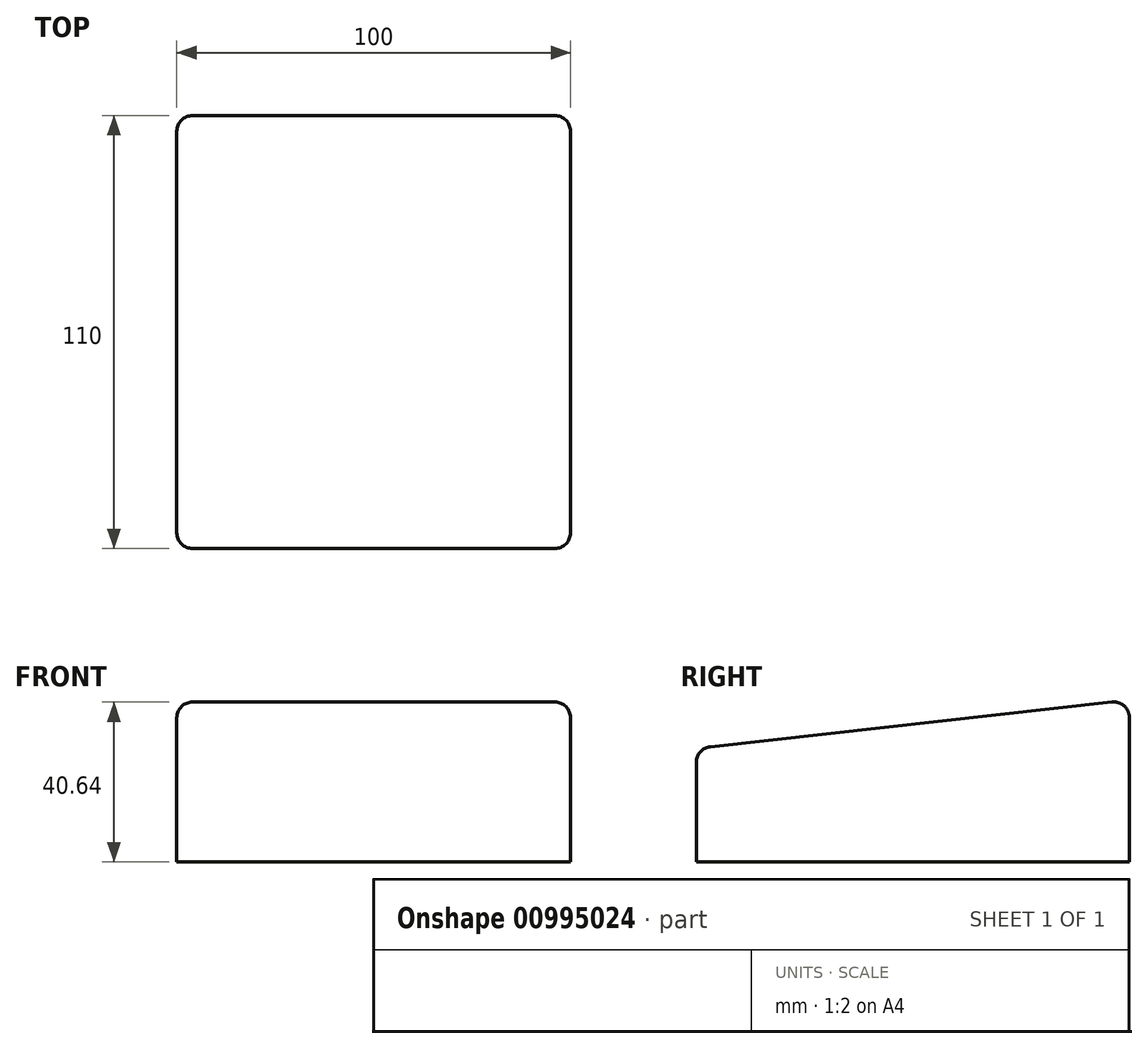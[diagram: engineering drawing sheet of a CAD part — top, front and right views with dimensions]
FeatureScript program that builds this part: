
annotation { "Feature Type Name" : "Feature", "Feature Type Description" : "" }
export const myFeature = defineFeature(function(context is Context, id is Id, definition is map)
    precondition{}
    {
        {
            var Q0;
            Q0=qCreatedBy(makeId("Right.planeOp"),FACE);
            var sketch = newSketch(context, id + "F0", { "sketchPlane" : qUnion([Q0])});
            skLineSegment(sketch, "E0", {"start": v(-55, 0) * mm, "end": v(55, 0) * mm});
            skLineSegment(sketch, "E1", {"start": v(55, 0) * mm, "end": v(55, 41.11) * mm});
            skLineSegment(sketch, "E2", {"start": v(55, 41.11) * mm, "end": v(-55, 28.89) * mm});
            skLineSegment(sketch, "E3", {"start": v(-55, 28.89) * mm, "end": v(-55, 0) * mm});
            skPoint(sketch, "E4", {"position": v(45, 40) * mm});
            skPoint(sketch, "E5", {"position": v(-45, 30) * mm});
            skPoint(sketch, "E6", {"position": v(0, 0) * mm});
            skLineSegment(sketch, "E7.0", {"start": v(55.22, 39.12) * mm, "end": v(-54.78, 26.9) * mm, "construction": true});
            skSolve(sketch);
        }
        {
            var Q0;
            Q0=qCreatedBy(makeId("Right.planeOp"),FACE);
            var sketch = newSketch(context, id + "F1", { "sketchPlane" : qUnion([Q0])});
            skCircle(sketch, "E8", {"center": v(7, 28.5) * mm, "radius": 27.5 * mm});
            skLineSegment(sketch, "E9", {"start": v(7, 28.5) * mm, "end": v(43.16, 27.87) * mm});
            skLineSegment(sketch, "E10", {"start": v(30.75, 37.09) * mm, "end": v(50.45, 36.74) * mm});
            skLineSegment(sketch, "E11", {"start": v(26.94, 18.15) * mm, "end": v(48.11, 17.78) * mm});
            skArc(sketch, "E12", {"start": v(32.12, 12.29) * mm, "mid": v(36.9, 29.25) * mm, "end": v(31.28, 45.94) * mm, "construction": true});
            skLineSegment(sketch, "E13", {"start": v(40.45, 36.92) * mm, "end": v(40.12, 17.92) * mm, "construction": true});
            skPoint(sketch, "E14", {"position": v(34.5, 28.02) * mm});
            skLineSegment(sketch, "E15", {"start": v(42.05, 36.89) * mm, "end": v(41.72, 17.9) * mm, "construction": true});
            skLineSegment(sketch, "E16", {"start": v(7, 28.5) * mm, "end": v(7, 15.35) * mm});
            skLineSegment(sketch, "E17", {"start": v(34.5, 28.02) * mm, "end": v(34.6, 33.85) * mm, "construction": true});
            skSolve(sketch);
        }
        {
            var Q0;
            Q0=sQuery(id+"F1.wireOp",VERTEX,"E9.start");
            var Q1;
            Q1=qCreatedBy(makeId("Top.planeOp"),FACE);
            cPlane(context, id + "F2", {"entities" : qUnion([Q0, Q1]), "cplaneType" : CPlaneType.PLANE_POINT, "offset" : 25 * mm, "width" : 150 * mm, "height" : 150 * mm});
        }
        {
            var Q0;
            Q0=sQuery(id+"F0.wireOp",EDGE,"E2");
            cPlane(context, id + "F3", {"entities" : qUnion([Q0]), "cplaneType" : CPlaneType.LINE_ANGLE, "offset" : 25 * mm, "angle" : 0 * degree, "width" : 150 * mm, "height" : 150 * mm});
        }
        {
            var Q0;
            Q0=qCreatedBy(id+"F3.planeOp",FACE);
            var sketch = newSketch(context, id + "F4", { "sketchPlane" : qUnion([Q0])});
            skLineSegment(sketch, "E18.bottom", {"start": v(-50, -59.2) * mm, "end": v(50, -59.2) * mm});
            skLineSegment(sketch, "E18.top", {"start": v(-50, 51.47) * mm, "end": v(50, 51.47) * mm});
            skLineSegment(sketch, "E18.left", {"start": v(-50, -59.2) * mm, "end": v(-50, 51.47) * mm});
            skLineSegment(sketch, "E18.right", {"start": v(50, -59.2) * mm, "end": v(50, 51.47) * mm});
            skPoint(sketch, "E19", {"position": v(0, 51.47) * mm});
            skSolve(sketch);
        }
        {
            var Q0;
            Q0=qCreatedBy(makeId("Front.planeOp"),FACE);
            var Q1;
            Q1=sQuery(id+"F1.wireOp",VERTEX,"E9.start");
            cPlane(context, id + "F5", {"entities" : qUnion([Q0, Q1]), "cplaneType" : CPlaneType.PLANE_POINT, "offset" : 25 * mm, "width" : 150 * mm, "height" : 150 * mm});
        }
        {
            var Q0;
            Q0=qCreatedBy(makeId("Top.planeOp"),FACE);
            var Q1;
            Q1=qCreatedBy(makeId("Origin.pointOp"),VERTEX);
            cPlane(context, id + "F6", {"entities" : qUnion([Q0, Q1]), "cplaneType" : CPlaneType.PLANE_POINT, "offset" : 25 * mm, "width" : 150 * mm, "height" : 150 * mm});
        }
        {
            var Q0;
            Q0=qCreatedBy(id+"F6.planeOp",FACE);
            var sketch = newSketch(context, id + "F7", { "sketchPlane" : qUnion([Q0])});
            skLineSegment(sketch, "E20.0.0", {"start": v(50, -55) * mm, "end": v(-50, -55) * mm});
            skLineSegment(sketch, "E20.0.1", {"start": v(-50, -55) * mm, "end": v(-50, 55) * mm});
            skLineSegment(sketch, "E20.0.2", {"start": v(-50, 55) * mm, "end": v(50, 55) * mm});
            skLineSegment(sketch, "E20.0.3", {"start": v(50, 55) * mm, "end": v(50, -55) * mm});
            skSolve(sketch);
        }
        {
            var Q0;
            Q0=qSketchRegion(id+"F0",true);
            var Q1;
            Q1=sQuery(id+"F7.wireOp",VERTEX,"E20.0.0.start");
            var Q2;
            Q2=sQuery(id+"F7.wireOp",VERTEX,"E20.0.0.end");
            extrude(context, id + "F8", {"entities" : qUnion([Q0]), "endBound" : BoundingType.UP_TO_VERTEX, "depth" : 25 * mm, "endBoundEntityVertex" : qUnion([Q1]), "offsetDistance" : 25 * mm, "hasSecondDirection" : true, "secondDirectionBound" : SecondDirectionBoundingType.UP_TO_VERTEX, "secondDirectionOppositeDirection" : true, "secondDirectionDepth" : 25 * mm, "secondDirectionBoundEntityVertex" : qUnion([Q2])});
        }
        {
            var Q0;
            Q0=makeQuery(id+"F8.opExtrude","CAP_EDGE",EDGE,{"disambiguationData":[OSD([sQuery(id+"F0.wireOp",EDGE,"E3")])],"isStart":false});
            var Q1;
            Q1=makeQuery(id+"F8.opExtrude","CAP_EDGE",EDGE,{"disambiguationData":[OSD([sQuery(id+"F0.wireOp",EDGE,"E3")])],"isStart":true});
            var Q2;
            Q2=makeQuery(id+"F8.opExtrude","CAP_EDGE",EDGE,{"disambiguationData":[OSD([sQuery(id+"F0.wireOp",EDGE,"E1")])],"isStart":false});
            var Q3;
            Q3=makeQuery(id+"F8.opExtrude","CAP_EDGE",EDGE,{"disambiguationData":[OSD([sQuery(id+"F0.wireOp",EDGE,"E1")])],"isStart":true});
            var Q4;
            Q4=makeQuery(id+"F8.opExtrude","SWEPT_FACE",FACE,{"disambiguationData":[OSD([sQuery(id+"F0.wireOp",EDGE,"E2")])]});
            fillet(context, id + "F9", {"entities" : qUnion([Q0, Q1, Q2, Q3, Q4]), "radius" : 4 * mm, "tangentPropagation" : true, "allowEdgeOverflow" : false});
        }
    });
